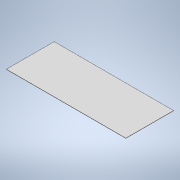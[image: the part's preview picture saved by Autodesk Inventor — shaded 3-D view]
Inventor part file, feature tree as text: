
AUTODESK INVENTOR PART (.ipt)
format: ipt  version: 2022 (Build 260153000, 153)  size: 92,672 bytes
history: native  units: mm
features: other x1, extrude x1, sketch x1
ambient origin geometry x8: Origin, YZ Plane, XZ Plane, XY Plane, X Axis, Y Axis, Z Axis, Center Point
bodies: Body1 (feature_tree)
feature tree (3):
  other  "Sólido1"
  extrude  "Extrusión1"  Depth=2000.0mm
  sketch  "Boceto1"  dims[d0=5000.0mm d1=2000.0mm d2=10.0mm d3=0.0mm]
